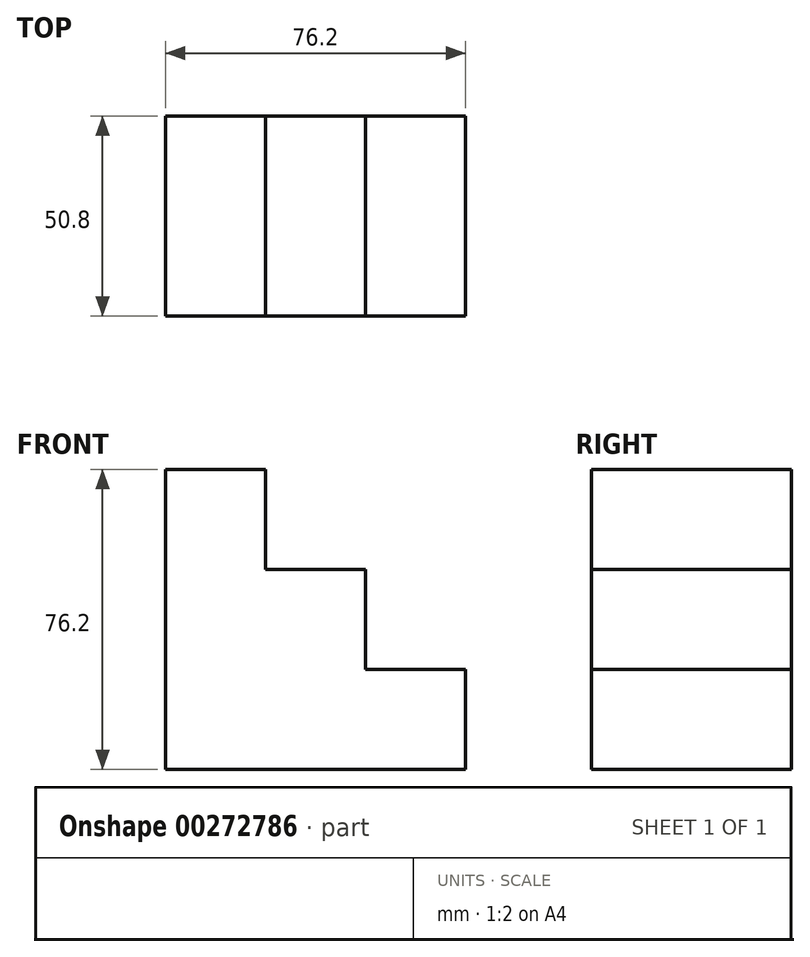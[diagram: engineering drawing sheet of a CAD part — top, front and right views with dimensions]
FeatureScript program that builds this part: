
annotation { "Feature Type Name" : "Feature", "Feature Type Description" : "" }
export const myFeature = defineFeature(function(context is Context, id is Id, definition is map)
    precondition{}
    {
        {
            var Q0;
            Q0=qCreatedBy(makeId("Front.planeOp"),FACE);
            var sketch = newSketch(context, id + "F0", { "sketchPlane" : qUnion([Q0])});
            skLineSegment(sketch, "E0", {"start": v(0, 0) * mm, "end": v(-76.2, 0) * mm});
            skLineSegment(sketch, "E1", {"start": v(-76.2, 0) * mm, "end": v(-76.2, 76.2) * mm});
            skLineSegment(sketch, "E2", {"start": v(-76.2, 76.2) * mm, "end": v(-50.8, 76.2) * mm});
            skLineSegment(sketch, "E3", {"start": v(-50.8, 76.2) * mm, "end": v(-50.8, 50.8) * mm});
            skLineSegment(sketch, "E4", {"start": v(-50.8, 50.8) * mm, "end": v(-25.4, 50.8) * mm});
            skLineSegment(sketch, "E5", {"start": v(-25.4, 50.8) * mm, "end": v(-25.4, 25.4) * mm});
            skLineSegment(sketch, "E6", {"start": v(0, 25.4) * mm, "end": v(0, 0) * mm});
            skLineSegment(sketch, "E7", {"start": v(-25.4, 25.4) * mm, "end": v(0, 25.4) * mm});
            skSolve(sketch);
        }
        {
            var Q0;
            Q0 = qSketchRegion(id + "F0", true);
            extrude(context, id + "F1", {"entities" : qUnion([Q0]), "depth" : 50.8 * mm});
        }
    });
